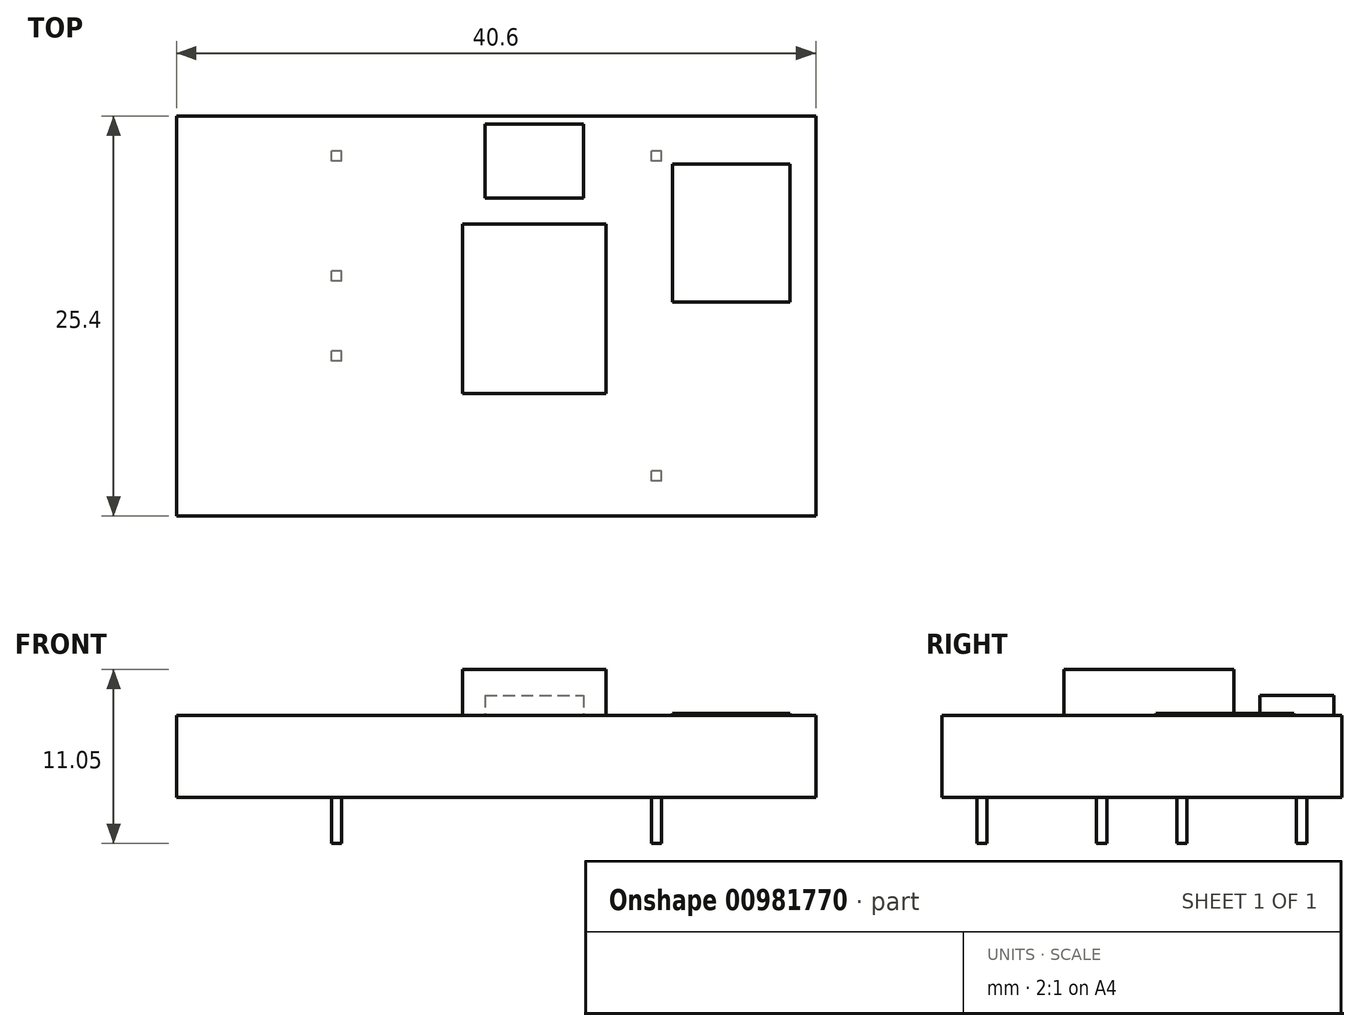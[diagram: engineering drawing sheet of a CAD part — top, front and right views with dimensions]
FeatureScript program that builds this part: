
annotation { "Feature Type Name" : "Feature", "Feature Type Description" : "" }
export const myFeature = defineFeature(function(context is Context, id is Id, definition is map)
    precondition{}
    {
        {
            var Q0;
            Q0=qCreatedBy(makeId("Top.planeOp"),FACE);
            var sketch = newSketch(context, id + "F0", { "sketchPlane" : qUnion([Q0])});
            skLineSegment(sketch, "E0.bottom", {"start": v(20.3, 12.7) * mm, "end": v(-20.3, 12.7) * mm});
            skLineSegment(sketch, "E0.top", {"start": v(20.3, -12.7) * mm, "end": v(-20.3, -12.7) * mm});
            skLineSegment(sketch, "E0.left", {"start": v(20.3, 12.7) * mm, "end": v(20.3, -12.7) * mm});
            skLineSegment(sketch, "E0.right", {"start": v(-20.3, 12.7) * mm, "end": v(-20.3, -12.7) * mm});
            skPoint(sketch, "E0.middle", {"position": v(0, 0) * mm});
            skLineSegment(sketch, "E1.bottom", {"start": v(-9.82, 9.84) * mm, "end": v(-10.46, 9.84) * mm});
            skLineSegment(sketch, "E1.top", {"start": v(-9.82, 10.48) * mm, "end": v(-10.46, 10.48) * mm});
            skLineSegment(sketch, "E1.left", {"start": v(-9.82, 9.84) * mm, "end": v(-9.82, 10.48) * mm});
            skLineSegment(sketch, "E1.right", {"start": v(-10.46, 9.84) * mm, "end": v(-10.46, 10.48) * mm});
            skPoint(sketch, "E1.middle", {"position": v(-10.14, 10.16) * mm});
            skLineSegment(sketch, "E2.bottom", {"start": v(-9.82, 2.22) * mm, "end": v(-10.46, 2.22) * mm});
            skLineSegment(sketch, "E2.top", {"start": v(-9.82, 2.86) * mm, "end": v(-10.46, 2.86) * mm});
            skLineSegment(sketch, "E2.left", {"start": v(-9.82, 2.22) * mm, "end": v(-9.82, 2.86) * mm});
            skLineSegment(sketch, "E2.right", {"start": v(-10.46, 2.22) * mm, "end": v(-10.46, 2.86) * mm});
            skPoint(sketch, "E2.middle", {"position": v(-10.14, 2.54) * mm});
            skLineSegment(sketch, "E3.bottom", {"start": v(-9.82, -2.86) * mm, "end": v(-10.46, -2.86) * mm});
            skLineSegment(sketch, "E3.top", {"start": v(-9.82, -2.22) * mm, "end": v(-10.46, -2.22) * mm});
            skLineSegment(sketch, "E3.left", {"start": v(-9.82, -2.86) * mm, "end": v(-9.82, -2.22) * mm});
            skLineSegment(sketch, "E3.right", {"start": v(-10.46, -2.86) * mm, "end": v(-10.46, -2.22) * mm});
            skPoint(sketch, "E3.middle", {"position": v(-10.14, -2.54) * mm});
            skLineSegment(sketch, "E4.bottom", {"start": v(10.5, 9.84) * mm, "end": v(9.86, 9.84) * mm});
            skLineSegment(sketch, "E4.top", {"start": v(10.5, 10.48) * mm, "end": v(9.86, 10.48) * mm});
            skLineSegment(sketch, "E4.left", {"start": v(10.5, 9.84) * mm, "end": v(10.5, 10.48) * mm});
            skLineSegment(sketch, "E4.right", {"start": v(9.86, 9.84) * mm, "end": v(9.86, 10.48) * mm});
            skPoint(sketch, "E4.middle", {"position": v(10.18, 10.16) * mm});
            skLineSegment(sketch, "E5.bottom", {"start": v(10.5, -10.48) * mm, "end": v(9.86, -10.48) * mm});
            skLineSegment(sketch, "E5.top", {"start": v(10.5, -9.84) * mm, "end": v(9.86, -9.84) * mm});
            skLineSegment(sketch, "E5.left", {"start": v(10.5, -10.48) * mm, "end": v(10.5, -9.84) * mm});
            skLineSegment(sketch, "E5.right", {"start": v(9.86, -10.48) * mm, "end": v(9.86, -9.84) * mm});
            skPoint(sketch, "E5.middle", {"position": v(10.18, -10.16) * mm});
            skLineSegment(sketch, "E6.bottom", {"start": v(-2.13, 5.84) * mm, "end": v(6.97, 5.84) * mm});
            skLineSegment(sketch, "E6.top", {"start": v(-2.13, -4.93) * mm, "end": v(6.97, -4.93) * mm});
            skLineSegment(sketch, "E6.left", {"start": v(-2.13, 5.84) * mm, "end": v(-2.13, -4.93) * mm});
            skLineSegment(sketch, "E6.right", {"start": v(6.97, 5.84) * mm, "end": v(6.97, -4.93) * mm});
            skLineSegment(sketch, "E7.bottom", {"start": v(-0.7, 12.2) * mm, "end": v(5.53, 12.2) * mm});
            skLineSegment(sketch, "E7.top", {"start": v(-0.7, 7.5) * mm, "end": v(5.53, 7.5) * mm});
            skLineSegment(sketch, "E7.left", {"start": v(-0.7, 12.2) * mm, "end": v(-0.7, 7.5) * mm});
            skLineSegment(sketch, "E7.right", {"start": v(5.53, 12.2) * mm, "end": v(5.53, 7.5) * mm});
            skLineSegment(sketch, "E8.bottom", {"start": v(11.2, 9.65) * mm, "end": v(18.65, 9.65) * mm});
            skLineSegment(sketch, "E8.top", {"start": v(11.2, 0.89) * mm, "end": v(18.65, 0.89) * mm});
            skLineSegment(sketch, "E8.left", {"start": v(11.2, 9.65) * mm, "end": v(11.2, 0.89) * mm});
            skLineSegment(sketch, "E8.right", {"start": v(18.65, 9.65) * mm, "end": v(18.65, 0.89) * mm});
            skPoint(sketch, "E9", {"position": v(2.42, 7.5) * mm});
            skPoint(sketch, "E10", {"position": v(2.42, 5.84) * mm});
            skSolve(sketch);
        }
        {
            var Q0;
            Q0=makeQuery(id+"F0.imprint","IMPRINT",FACE,{"disambiguationData":[TD([[makeQuery(id+"F0.imprint","IMPRINT",EDGE,{"derivedFrom":sQuery(id+"F0.wireOp",EDGE,"E0.bottom")}),1.0]])]});
            var Q1;
            Q1=makeQuery(id+"F0.imprint","IMPRINT",FACE,{"disambiguationData":[TD([[makeQuery(id+"F0.imprint","IMPRINT",EDGE,{"derivedFrom":sQuery(id+"F0.wireOp",EDGE,"E1.bottom")}),-1.0]])]});
            var Q2;
            Q2=makeQuery(id+"F0.imprint","IMPRINT",FACE,{"disambiguationData":[TD([[makeQuery(id+"F0.imprint","IMPRINT",EDGE,{"derivedFrom":sQuery(id+"F0.wireOp",EDGE,"E2.bottom")}),-1.0]])]});
            var Q3;
            Q3=makeQuery(id+"F0.imprint","IMPRINT",FACE,{"disambiguationData":[TD([[makeQuery(id+"F0.imprint","IMPRINT",EDGE,{"derivedFrom":sQuery(id+"F0.wireOp",EDGE,"E3.bottom")}),-1.0]])]});
            var Q4;
            Q4=makeQuery(id+"F0.imprint","IMPRINT",FACE,{"disambiguationData":[TD([[makeQuery(id+"F0.imprint","IMPRINT",EDGE,{"derivedFrom":sQuery(id+"F0.wireOp",EDGE,"E4.bottom")}),-1.0]])]});
            var Q5;
            Q5=makeQuery(id+"F0.imprint","IMPRINT",FACE,{"disambiguationData":[TD([[makeQuery(id+"F0.imprint","IMPRINT",EDGE,{"derivedFrom":sQuery(id+"F0.wireOp",EDGE,"E5.bottom")}),-1.0]])]});
            extrude(context, id + "F1", {"entities" : qUnion([Q0, Q1, Q2, Q3, Q4, Q5]), "depth" : 2.67 * mm, "offsetDistance" : 25 * mm});
        }
        {
            var Q0;
            Q0=makeQuery(id+"F0.imprint","IMPRINT",FACE,{"disambiguationData":[TD([[makeQuery(id+"F0.imprint","IMPRINT",EDGE,{"derivedFrom":sQuery(id+"F0.wireOp",EDGE,"E6.bottom")}),-1.0]])]});
            extrude(context, id + "F2", {"entities" : qUnion([Q0]), "operationType" : NewBodyOperationType.ADD, "depth" : 5.6 * mm, "offsetDistance" : 25 * mm});
        }
        {
            var Q0;
            Q0=makeQuery(id+"F0.imprint","IMPRINT",FACE,{"disambiguationData":[TD([[makeQuery(id+"F0.imprint","IMPRINT",EDGE,{"derivedFrom":sQuery(id+"F0.wireOp",EDGE,"E7.bottom")}),-1.0]])]});
            extrude(context, id + "F3", {"entities" : qUnion([Q0]), "operationType" : NewBodyOperationType.ADD, "depth" : 3.94 * mm, "offsetDistance" : 25 * mm});
        }
        {
            var Q0;
            Q0=makeQuery(id+"F0.imprint","IMPRINT",FACE,{"disambiguationData":[TD([[makeQuery(id+"F0.imprint","IMPRINT",EDGE,{"derivedFrom":sQuery(id+"F0.wireOp",EDGE,"E8.bottom")}),-1.0]])]});
            extrude(context, id + "F4", {"entities" : qUnion([Q0]), "operationType" : NewBodyOperationType.ADD, "depth" : 2.8 * mm, "offsetDistance" : 25 * mm});
        }
        {
            var Q0;
            Q0=makeQuery(id+"F0.imprint","IMPRINT",FACE,{"disambiguationData":[TD([[makeQuery(id+"F0.imprint","IMPRINT",EDGE,{"derivedFrom":sQuery(id+"F0.wireOp",EDGE,"E0.bottom")}),1.0]])]});
            var Q1;
            Q1=makeQuery(id+"F0.imprint","IMPRINT",FACE,{"disambiguationData":[TD([[makeQuery(id+"F0.imprint","IMPRINT",EDGE,{"derivedFrom":sQuery(id+"F0.wireOp",EDGE,"E3.bottom")}),-1.0]])]});
            var Q2;
            Q2=makeQuery(id+"F0.imprint","IMPRINT",FACE,{"disambiguationData":[TD([[makeQuery(id+"F0.imprint","IMPRINT",EDGE,{"derivedFrom":sQuery(id+"F0.wireOp",EDGE,"E2.bottom")}),-1.0]])]});
            var Q3;
            Q3=makeQuery(id+"F0.imprint","IMPRINT",FACE,{"disambiguationData":[TD([[makeQuery(id+"F0.imprint","IMPRINT",EDGE,{"derivedFrom":sQuery(id+"F0.wireOp",EDGE,"E1.bottom")}),-1.0]])]});
            var Q4;
            Q4=makeQuery(id+"F0.imprint","IMPRINT",FACE,{"disambiguationData":[TD([[makeQuery(id+"F0.imprint","IMPRINT",EDGE,{"derivedFrom":sQuery(id+"F0.wireOp",EDGE,"E4.bottom")}),-1.0]])]});
            var Q5;
            Q5=makeQuery(id+"F0.imprint","IMPRINT",FACE,{"disambiguationData":[TD([[makeQuery(id+"F0.imprint","IMPRINT",EDGE,{"derivedFrom":sQuery(id+"F0.wireOp",EDGE,"E7.bottom")}),-1.0]])]});
            var Q6;
            Q6=makeQuery(id+"F0.imprint","IMPRINT",FACE,{"disambiguationData":[TD([[makeQuery(id+"F0.imprint","IMPRINT",EDGE,{"derivedFrom":sQuery(id+"F0.wireOp",EDGE,"E6.bottom")}),-1.0]])]});
            var Q7;
            Q7=makeQuery(id+"F0.imprint","IMPRINT",FACE,{"disambiguationData":[TD([[makeQuery(id+"F0.imprint","IMPRINT",EDGE,{"derivedFrom":sQuery(id+"F0.wireOp",EDGE,"E8.bottom")}),-1.0]])]});
            var Q8;
            Q8=makeQuery(id+"F0.imprint","IMPRINT",FACE,{"disambiguationData":[TD([[makeQuery(id+"F0.imprint","IMPRINT",EDGE,{"derivedFrom":sQuery(id+"F0.wireOp",EDGE,"E5.bottom")}),-1.0]])]});
            extrude(context, id + "F5", {"entities" : qUnion([Q0, Q1, Q2, Q3, Q4, Q5, Q6, Q7, Q8]), "operationType" : NewBodyOperationType.ADD, "oppositeDirection" : true, "depth" : 2.54 * mm, "offsetDistance" : 25 * mm});
        }
        {
            var Q0;
            Q0=makeQuery(id+"F0.imprint","IMPRINT",FACE,{"disambiguationData":[TD([[makeQuery(id+"F0.imprint","IMPRINT",EDGE,{"derivedFrom":sQuery(id+"F0.wireOp",EDGE,"E3.bottom")}),-1.0]])]});
            var Q1;
            Q1=makeQuery(id+"F0.imprint","IMPRINT",FACE,{"disambiguationData":[TD([[makeQuery(id+"F0.imprint","IMPRINT",EDGE,{"derivedFrom":sQuery(id+"F0.wireOp",EDGE,"E2.bottom")}),-1.0]])]});
            var Q2;
            Q2=makeQuery(id+"F0.imprint","IMPRINT",FACE,{"disambiguationData":[TD([[makeQuery(id+"F0.imprint","IMPRINT",EDGE,{"derivedFrom":sQuery(id+"F0.wireOp",EDGE,"E1.bottom")}),-1.0]])]});
            var Q3;
            Q3=makeQuery(id+"F0.imprint","IMPRINT",FACE,{"disambiguationData":[TD([[makeQuery(id+"F0.imprint","IMPRINT",EDGE,{"derivedFrom":sQuery(id+"F0.wireOp",EDGE,"E4.bottom")}),-1.0]])]});
            var Q4;
            Q4=makeQuery(id+"F0.imprint","IMPRINT",FACE,{"disambiguationData":[TD([[makeQuery(id+"F0.imprint","IMPRINT",EDGE,{"derivedFrom":sQuery(id+"F0.wireOp",EDGE,"E5.bottom")}),-1.0]])]});
            extrude(context, id + "F6", {"entities" : qUnion([Q0, Q1, Q2, Q3, Q4]), "operationType" : NewBodyOperationType.ADD, "oppositeDirection" : true, "depth" : 5.46 * mm, "offsetDistance" : 25 * mm});
        }
    });
